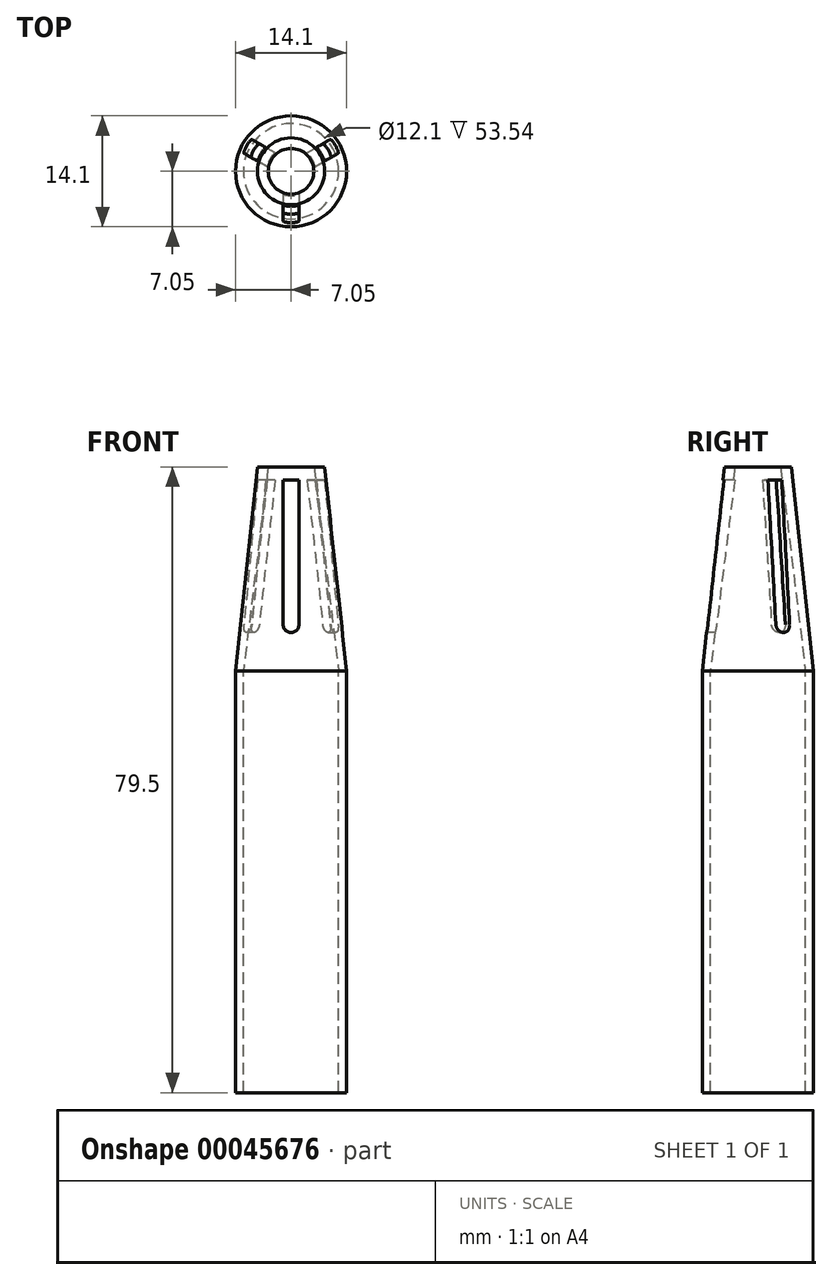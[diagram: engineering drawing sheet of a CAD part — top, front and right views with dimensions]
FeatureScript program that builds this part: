
annotation { "Feature Type Name" : "Feature", "Feature Type Description" : "" }
export const myFeature = defineFeature(function(context is Context, id is Id, definition is map)
    precondition{}
    {
        {
            var Q0;
            Q0=qCreatedBy(makeId("Top.planeOp"),FACE);
            var sketch = newSketch(context, id + "F0", { "sketchPlane" : qUnion([Q0])});
            skCircle(sketch, "E0", {"center": v(0, 0) * mm, "radius": 7.05 * mm});
            skSolve(sketch);
        }
        {
            var Q0;
            Q0=makeQuery(id+"F0.imprint","IMPRINT",FACE,{"disambiguationData":[TD([[makeQuery(id+"F0.imprint","IMPRINT",EDGE,{"derivedFrom":sQuery(id+"F0.wireOp",EDGE,"E0")}),1.0]])]});
            cPlane(context, id + "F1", {"entities" : qUnion([Q0]), "cplaneType" : CPlaneType.OFFSET, "offset" : 25.96 * mm, "width" : 150 * mm, "height" : 150 * mm});
        }
        {
            var Q0;
            Q0=qCreatedBy(id+"F1.planeOp",FACE);
            var sketch = newSketch(context, id + "F2", { "sketchPlane" : qUnion([Q0])});
            skCircle(sketch, "E1", {"center": v(0, 0) * mm, "radius": 4.25 * mm});
            skSolve(sketch);
        }
        {
            var Q0;
            Q0 = qSketchRegion(id + "F2", true);
            var Q1;
            Q1 = qSketchRegion(id + "F0", true);
            loft(context, id + "F3", {"sheetProfilesArray" : [{ "sheetProfileEntities" : qUnion([Q0]) }, { "sheetProfileEntities" : qUnion([Q1]) }]});
        }
        {
            var Q0;
            Q0=makeQuery(id+"F3.opLoft","CAP_FACE",FACE,{"disambiguationData":[OSD([makeQuery(id+"F0.imprint","IMPRINT",FACE,{"disambiguationData":[TD([[makeQuery(id+"F0.imprint","IMPRINT",EDGE,{"derivedFrom":sQuery(id+"F0.wireOp",EDGE,"E0")}),1.0]])]})])],"isStart":true});
            var sketch = newSketch(context, id + "F4", { "sketchPlane" : qUnion([Q0])});
            skCircle(sketch, "E2", {"center": v(0, 0) * mm, "radius": 6.05 * mm});
            skSolve(sketch);
        }
        {
            var Q0;
            Q0=makeQuery(id+"F3.opLoft","CAP_FACE",FACE,{"disambiguationData":[OSD([makeQuery(id+"F2.imprint","IMPRINT",FACE,{"disambiguationData":[TD([[makeQuery(id+"F2.imprint","IMPRINT",EDGE,{"derivedFrom":sQuery(id+"F2.wireOp",EDGE,"E1")}),1.0]])]})])],"isStart":true});
            var sketch = newSketch(context, id + "F5", { "sketchPlane" : qUnion([Q0])});
            skCircle(sketch, "E3", {"center": v(0, 0) * mm, "radius": 2.9 * mm});
            skSolve(sketch);
        }
        {
            var Q1;
            Q1 = qSketchRegion(id + "F5", true);
            var Q2;
            Q2 = qSketchRegion(id + "F4", true);
            loft(context, id + "F6", {"operationType" : NewBodyOperationType.REMOVE, "sheetProfilesArray" : [{ "sheetProfileEntities" : qUnion([Q1]) }, { "sheetProfileEntities" : qUnion([Q2]) }]});
        }
        {
            var Q0;
            Q0=makeQuery(id+"F3.opLoft","CAP_FACE",FACE,{"disambiguationData":[OSD([makeQuery(id+"F0.imprint","IMPRINT",FACE,{"disambiguationData":[TD([[makeQuery(id+"F0.imprint","IMPRINT",EDGE,{"derivedFrom":sQuery(id+"F0.wireOp",EDGE,"E0")}),1.0]])]})])],"isStart":true});
            extrude(context, id + "F7", {"entities" : qUnion([Q0]), "operationType" : NewBodyOperationType.ADD, "depth" : 53.54 * mm});
        }
        {
            var Q0;
            Q0=qCreatedBy(makeId("Front.planeOp"),FACE);
            cPlane(context, id + "F8", {"entities" : qUnion([Q0]), "cplaneType" : CPlaneType.OFFSET, "offset" : 4 * mm, "width" : 150 * mm, "height" : 150 * mm});
        }
        {
            var Q0;
            Q0=qCreatedBy(id+"F8.planeOp",FACE);
            var sketch = newSketch(context, id + "F9", { "sketchPlane" : qUnion([Q0])});
            skLineSegment(sketch, "E4.rect.bottom", {"start": v(1.01, 24.3) * mm, "end": v(-1.01, 24.3) * mm});
            skLineSegment(sketch, "E4.rect.top", {"start": v(1.01, 5.93) * mm, "end": v(-1.01, 5.93) * mm});
            skLineSegment(sketch, "E4.rect.left", {"start": v(1.01, 24.3) * mm, "end": v(1.01, 5.93) * mm});
            skLineSegment(sketch, "E4.rect.right", {"start": v(-1.01, 24.3) * mm, "end": v(-1.01, 5.93) * mm});
            skPoint(sketch, "E4.rect.middle", {"position": v(0, 15.12) * mm});
            skArc(sketch, "E5", {"start": v(-1.01, 5.93) * mm, "mid": v(0, 4.92) * mm, "end": v(1.02, 5.93) * mm});
            skSolve(sketch);
        }
        {
            var Q0;
            Q0 = qSketchRegion(id + "F9", true);
            extrude(context, id + "F10", {"entities" : qUnion([Q0]), "depth" : 15.84 * mm, "hasSecondDirection" : true, "secondDirectionOppositeDirection" : true, "secondDirectionDepth" : 5.3 * mm});
        }
        {
            var Q0;
            Q0=qCreatedBy(makeId("Right.planeOp"),FACE);
            var sketch = newSketch(context, id + "F11", { "sketchPlane" : qUnion([Q0])});
            skLineSegment(sketch, "E6", {"start": v(0, 0) * mm, "end": v(0, 49.73) * mm, "construction": true});
            skSolve(sketch);
        }
        {
            var Q0;
            Q0=makeQuery(id+"F10.opExtrude","SWEPT_BODY",BODY,{"disambiguationData":[OSD([sQuery(id+"F9.wireOp",EDGE,"E4.rect.bottom"),sQuery(id+"F9.wireOp",EDGE,"E4.rect.left"),sQuery(id+"F9.wireOp",EDGE,"E4.rect.right"),sQuery(id+"F9.wireOp",EDGE,"E5")])]});
            var Q1;
            Q1=sQuery(id+"F11.wireOp",EDGE,"E6");
            circularPattern(context, id + "F12", {"entities" : qUnion([Q0]), "axis" : qUnion([Q1]), "angle" : 120 * degree, "instanceCount" : 3});
        }
        {
            var Q0;
            Q0=makeQuery(id+"F12.opPattern","COPY",FACE,{"derivedFrom":makeQuery(id+"F10.opExtrude","CAP_FACE",FACE,{"disambiguationData":[OSD([sQuery(id+"F9.wireOp",EDGE,"E4.rect.bottom"),sQuery(id+"F9.wireOp",EDGE,"E4.rect.left"),sQuery(id+"F9.wireOp",EDGE,"E4.rect.right"),sQuery(id+"F9.wireOp",EDGE,"E5")])],"isStart":false}),"instanceName":"1"});
            var sketch = newSketch(context, id + "F13", { "sketchPlane" : qUnion([Q0])});
            skLineSegment(sketch, "E7.0.0", {"start": v(1.02, 5.93) * mm, "end": v(1.02, 24.3) * mm});
            skLineSegment(sketch, "E7.0.1", {"start": v(1.02, 24.3) * mm, "end": v(-1.01, 24.3) * mm});
            skLineSegment(sketch, "E7.0.2", {"start": v(-1.01, 24.3) * mm, "end": v(-1.01, 5.93) * mm});
            skArc(sketch, "E7.0.3", {"start": v(-1.02, 5.93) * mm, "mid": v(0, 4.92) * mm, "end": v(1.02, 5.93) * mm});
            skSolve(sketch);
        }
        {
            var Q0;
            Q0 = qSketchRegion(id + "F13", true);
            extrude(context, id + "F14", {"entities" : qUnion([Q0]), "operationType" : NewBodyOperationType.REMOVE, "oppositeDirection" : true, "depth" : 22 * mm});
        }
        {
            var Q0;
            Q0=makeQuery(id+"F12.opPattern","COPY",FACE,{"derivedFrom":makeQuery(id+"F10.opExtrude","CAP_FACE",FACE,{"disambiguationData":[OSD([sQuery(id+"F9.wireOp",EDGE,"E4.rect.bottom"),sQuery(id+"F9.wireOp",EDGE,"E4.rect.left"),sQuery(id+"F9.wireOp",EDGE,"E4.rect.right"),sQuery(id+"F9.wireOp",EDGE,"E5")])],"isStart":false}),"instanceName":"2"});
            var sketch = newSketch(context, id + "F15", { "sketchPlane" : qUnion([Q0])});
            skLineSegment(sketch, "E8.0.0", {"start": v(1.02, 5.93) * mm, "end": v(1.02, 24.3) * mm});
            skLineSegment(sketch, "E8.0.1", {"start": v(1.02, 24.3) * mm, "end": v(-1.01, 24.3) * mm});
            skLineSegment(sketch, "E8.0.2", {"start": v(-1.01, 24.3) * mm, "end": v(-1.01, 5.93) * mm});
            skArc(sketch, "E8.0.3", {"start": v(-1.02, 5.93) * mm, "mid": v(0, 4.92) * mm, "end": v(1.02, 5.93) * mm});
            skSolve(sketch);
        }
        {
            var Q0;
            Q0 = qSketchRegion(id + "F15", true);
            extrude(context, id + "F16", {"entities" : qUnion([Q0]), "operationType" : NewBodyOperationType.REMOVE, "oppositeDirection" : true, "depth" : 22 * mm});
        }
        {
            var Q0;
            Q0=makeQuery(id+"F10.opExtrude","CAP_FACE",FACE,{"disambiguationData":[OSD([sQuery(id+"F9.wireOp",EDGE,"E4.rect.bottom"),sQuery(id+"F9.wireOp",EDGE,"E4.rect.left"),sQuery(id+"F9.wireOp",EDGE,"E4.rect.right"),sQuery(id+"F9.wireOp",EDGE,"E5")])],"isStart":false});
            var sketch = newSketch(context, id + "F17", { "sketchPlane" : qUnion([Q0])});
            skLineSegment(sketch, "E9.0.0", {"start": v(1.01, 5.93) * mm, "end": v(1.01, 24.3) * mm});
            skLineSegment(sketch, "E9.0.1", {"start": v(1.01, 24.3) * mm, "end": v(-1.01, 24.3) * mm});
            skLineSegment(sketch, "E9.0.2", {"start": v(-1.01, 24.3) * mm, "end": v(-1.01, 5.93) * mm});
            skArc(sketch, "E9.0.3", {"start": v(-1.01, 5.93) * mm, "mid": v(0, 4.92) * mm, "end": v(1.02, 5.93) * mm});
            skSolve(sketch);
        }
        {
            var Q0;
            Q0=makeQuery(id+"F17.imprint","IMPRINT",FACE,{"disambiguationData":[TD([[makeQuery(id+"F17.imprint","IMPRINT",EDGE,{"derivedFrom":sQuery(id+"F17.wireOp",EDGE,"E9.0.0")}),-1.0]])]});
            extrude(context, id + "F18", {"entities" : qUnion([Q0]), "operationType" : NewBodyOperationType.REMOVE, "oppositeDirection" : true, "depth" : 22 * mm});
        }
    });
